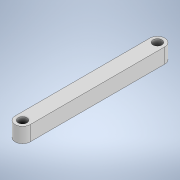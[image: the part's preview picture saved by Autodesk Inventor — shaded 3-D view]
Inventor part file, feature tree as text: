
AUTODESK INVENTOR PART (.ipt)
format: ipt  version: 2022 (Build 260153000, 153)  size: 99,328 bytes
history: native  units: mm
features: extrude x1, sketch x1
ambient origin geometry x8: Origin, YZ Plane, XZ Plane, XY Plane, X Axis, Y Axis, Z Axis, Center Point
bodies: Solid1 (feature_tree)
feature tree (2):
  extrude  "Extrusion1"  Depth=5.0mm
  sketch  "Sketch1"  dims[d2=3.0mm d3=3.0mm d4=5.0mm d5=0.0mm]
